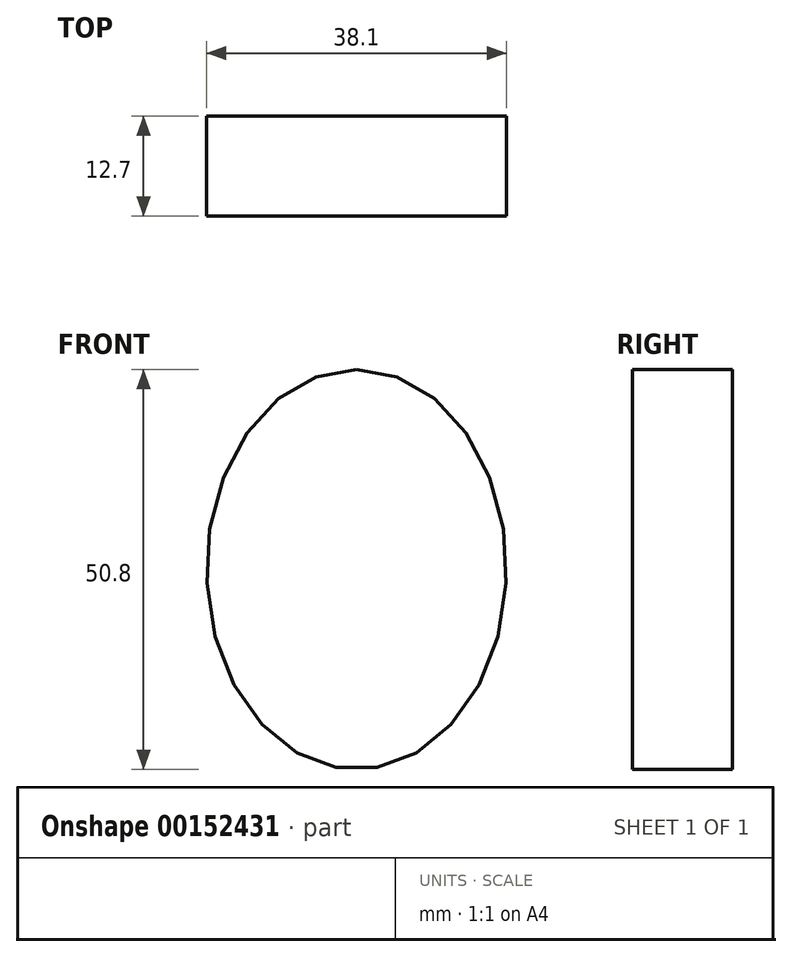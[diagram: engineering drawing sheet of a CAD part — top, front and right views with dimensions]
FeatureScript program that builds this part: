
annotation { "Feature Type Name" : "Feature", "Feature Type Description" : "" }
export const myFeature = defineFeature(function(context is Context, id is Id, definition is map)
    precondition{}
    {
        {
            var Q0;
            Q0=qCreatedBy(makeId("Front.planeOp"),FACE);
            var sketch = newSketch(context, id + "F0", { "sketchPlane" : qUnion([Q0])});
            skEllipse(sketch, "E0", {"center": v(0, 0) * mm, "majorRadius": 25.4 * mm, "minorRadius": 19.05 * mm, "majorAxis": v(0, 1)});
            skLineSegment(sketch, "E1", {"start": v(0, 25.4) * mm, "end": v(29.98, 25.4) * mm, "construction": true});
            skSolve(sketch);
        }
        {
            var Q0;
            Q0=makeQuery(id+"F0.imprint","IMPRINT",FACE,{"disambiguationData":[TD([[makeQuery(id+"F0.imprint","IMPRINT",EDGE,{"derivedFrom":sQuery(id+"F0.wireOp",EDGE,"E0")}),1.0]])]});
            extrude(context, id + "F1", {"entities" : qUnion([Q0]), "depth" : 12.7 * mm});
        }
        {
            var Q0;
            Q0=makeQuery(id+"F1.opExtrude","CAP_FACE",FACE,{"disambiguationData":[OSD([sQuery(id+"F0.wireOp",EDGE,"E0")])],"isStart":false});
            var sketch = newSketch(context, id + "F2", { "sketchPlane" : qUnion([Q0])});
            skCircle(sketch, "E2", {"center": v(0, 0) * mm, "radius": 6.6 * mm});
            skSolve(sketch);
        }
        {
            var Q0;
            Q0=makeQuery(id+"F2.imprint","IMPRINT",FACE,{"disambiguationData":[TD([[makeQuery(id+"F2.imprint","IMPRINT",EDGE,{"derivedFrom":sQuery(id+"F2.wireOp",EDGE,"E2")}),1.0]])]});
            var Q1;
            Q1=sQuery(id+"F2.wireOp",EDGE,"E2");
            extrude(context, id + "F3", {"entities" : qUnion([Q0]), "operationType" : NewBodyOperationType.REMOVE, "surfaceEntities" : qUnion([Q1]), "endBound" : BoundingType.SYMMETRIC, "depth" : 25.4 * mm});
        }
        {
            var Q0;
            Q0=qCreatedBy(makeId("Front.planeOp"),FACE);
            var sketch = newSketch(context, id + "F4", { "sketchPlane" : qUnion([Q0])});
            skCircle(sketch, "E3", {"center": v(0, 0) * mm, "radius": 11.62 * mm});
            skSolve(sketch);
        }
        {
            var Q0;
            Q0 = qSketchRegion(id + "F4", true);
            extrude(context, id + "F5", {"entities" : qUnion([Q0]), "operationType" : NewBodyOperationType.ADD, "depth" : 12.7 * mm});
        }
    });
